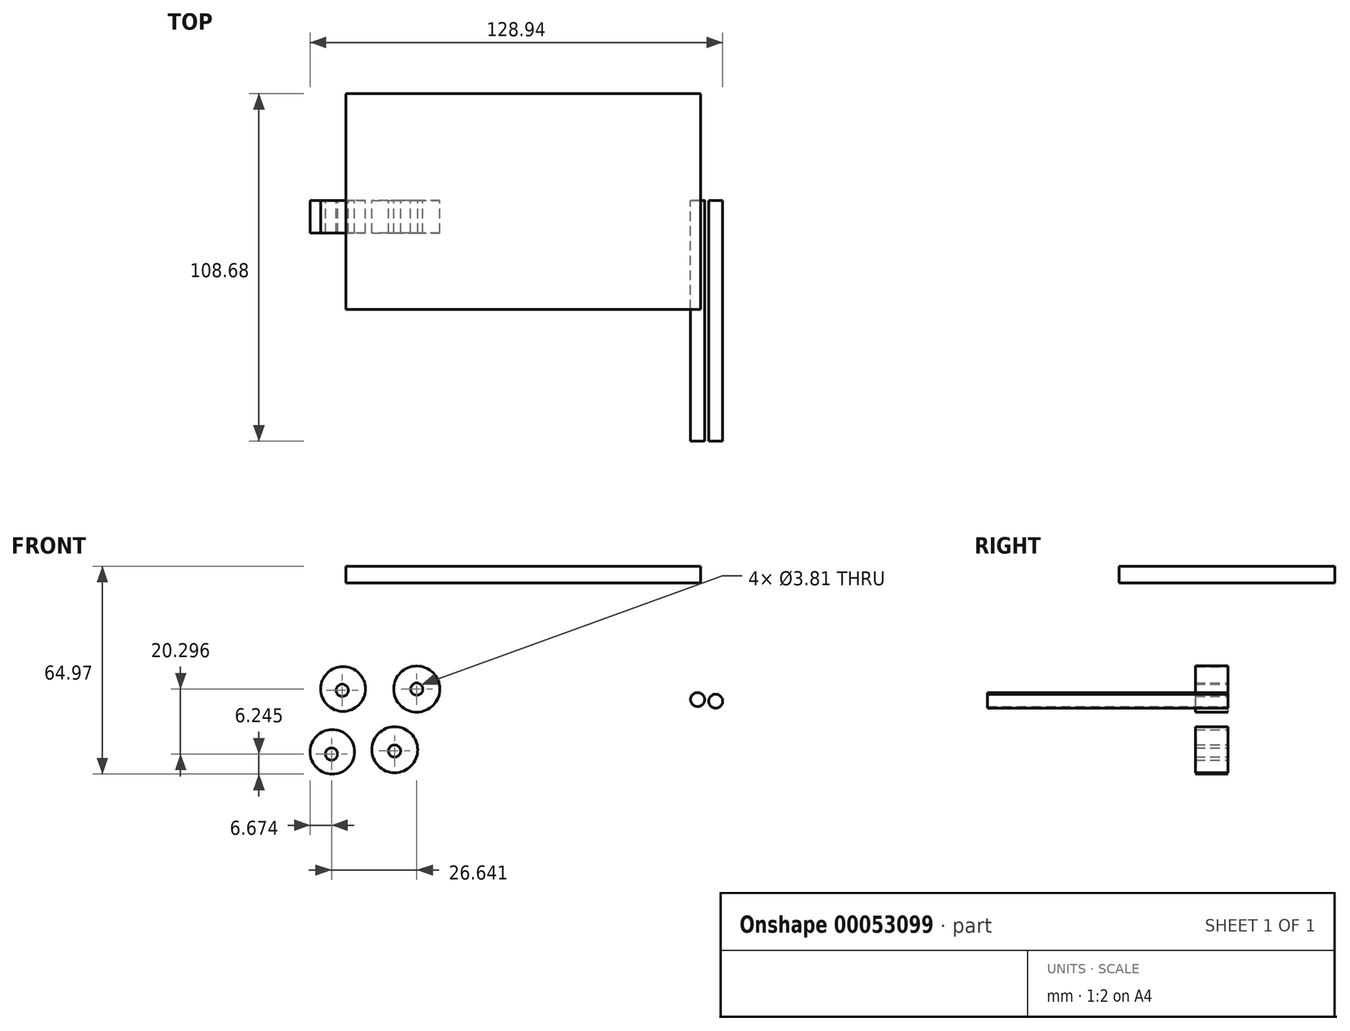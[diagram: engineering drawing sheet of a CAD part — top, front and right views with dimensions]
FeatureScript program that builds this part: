
annotation { "Feature Type Name" : "Feature", "Feature Type Description" : "" }
export const myFeature = defineFeature(function(context is Context, id is Id, definition is map)
    precondition{}
    {
        {
            var Q0;
            Q0=qCreatedBy(makeId("Top.planeOp"),FACE);
            var sketch = newSketch(context, id + "F0", { "sketchPlane" : qUnion([Q0])});
            skLineSegment(sketch, "E0.bottom", {"start": v(-58.44, 33.42) * mm, "end": v(52.35, 33.42) * mm});
            skLineSegment(sketch, "E0.top", {"start": v(-58.44, -34.06) * mm, "end": v(52.35, -34.06) * mm});
            skLineSegment(sketch, "E0.left", {"start": v(-58.44, 33.42) * mm, "end": v(-58.44, -34.06) * mm});
            skLineSegment(sketch, "E0.right", {"start": v(52.35, 33.42) * mm, "end": v(52.35, -34.06) * mm});
            skSolve(sketch);
        }
        {
            var Q0;
            Q0 = qSketchRegion(id + "F0", true);
            extrude(context, id + "F1", {"entities" : qUnion([Q0]), "depth" : 5.3 * mm});
        }
        {
            var Q0;
            Q0=qCreatedBy(makeId("Front.planeOp"),FACE);
            var sketch = newSketch(context, id + "F2", { "sketchPlane" : qUnion([Q0])});
            skCircle(sketch, "E1", {"center": v(57.1, -36.91) * mm, "radius": 2.18 * mm});
            skCircle(sketch, "E2", {"center": v(51.46, -36.4) * mm, "radius": 2.2 * mm});
            skSolve(sketch);
        }
        {
            var Q0;
            Q0 = qSketchRegion(id + "F2", true);
            extrude(context, id + "F3", {"entities" : qUnion([Q0]), "depth" : 75.26 * mm});
        }
        {
            var Q0;
            Q0=qCreatedBy(makeId("Front.planeOp"),FACE);
            var sketch = newSketch(context, id + "F4", { "sketchPlane" : qUnion([Q0])});
            skCircle(sketch, "E3", {"center": v(-53.68, -50.73) * mm, "radius": 7.69 * mm});
            skCircle(sketch, "E4", {"center": v(-34.72, -49.33) * mm, "radius": 8.01 * mm});
            skSolve(sketch);
        }
        {
            var Q0;
            Q0=makeQuery(id+"F4.imprint","IMPRINT",FACE,{"disambiguationData":[TD([[makeQuery(id+"F4.imprint","IMPRINT",EDGE,{"derivedFrom":sQuery(id+"F4.wireOp",EDGE,"E4")}),1.0]])]});
            var Q1;
            Q1=makeQuery(id+"F4.imprint","IMPRINT",FACE,{"disambiguationData":[TD([[makeQuery(id+"F4.imprint","IMPRINT",EDGE,{"derivedFrom":sQuery(id+"F4.wireOp",EDGE,"E3")}),1.0]])]});
            extrude(context, id + "F5", {"entities" : qUnion([Q0, Q1]), "depth" : 10.16 * mm});
        }
        {
            var Q0;
            Q0=makeQuery(id+"F5.opExtrude","SWEPT_BODY",BODY,{"disambiguationData":[OSD([sQuery(id+"F4.wireOp",EDGE,"E3")])]});
            deleteBodies(context, id + "F6", {"entities" : qUnion([Q0])});
        }
        {
            var Q0;
            Q0=makeQuery(id+"F5.opExtrude","SWEPT_BODY",BODY,{"disambiguationData":[OSD([sQuery(id+"F4.wireOp",EDGE,"E4")])]});
            deleteBodies(context, id + "F7", {"entities" : qUnion([Q0])});
        }
        {
            var Q0;
            Q0=qCreatedBy(makeId("Front.planeOp"),FACE);
            var sketch = newSketch(context, id + "F8", { "sketchPlane" : qUnion([Q0])});
            skCircle(sketch, "E5", {"center": v(-62.71, -52.75) * mm, "radius": 6.94 * mm});
            skCircle(sketch, "E6", {"center": v(-43.2, -52.1) * mm, "radius": 7.18 * mm});
            skCircle(sketch, "E7", {"center": v(-59.37, -33.1) * mm, "radius": 6.99 * mm});
            skCircle(sketch, "E8", {"center": v(-36.33, -33.14) * mm, "radius": 7.22 * mm});
            skSolve(sketch);
        }
        {
            var Q0;
            Q0 = qSketchRegion(id + "F8", true);
            extrude(context, id + "F9", {"entities" : qUnion([Q0]), "depth" : 10.16 * mm});
        }
        {
            var Q0;
            Q0=makeQuery(id+"F9.opExtrude","CAP_FACE",FACE,{"disambiguationData":[OSD([sQuery(id+"F8.wireOp",EDGE,"E8")])],"isStart":true});
            var sketch = newSketch(context, id + "F10", { "sketchPlane" : qUnion([Q0])});
            skPoint(sketch, "E9", {"position": v(59.62, -33.51) * mm});
            skPoint(sketch, "E10", {"position": v(62.98, -53.44) * mm});
            skPoint(sketch, "E11", {"position": v(36.33, -33.14) * mm});
            skPoint(sketch, "E12", {"position": v(43.27, -52.48) * mm});
            skSolve(sketch);
        }
        {
            var Q0;
            Q0=sQuery(id+"F10.wireOp",VERTEX,"E11");
            var Q1;
            Q1=sQuery(id+"F10.wireOp",VERTEX,"E9");
            var Q2;
            Q2=sQuery(id+"F10.wireOp",VERTEX,"E10");
            var Q3;
            Q3=sQuery(id+"F10.wireOp",VERTEX,"E12");
            var Q4;
            Q4=makeQuery(id+"F9.opExtrude","SWEPT_BODY",BODY,{"disambiguationData":[OSD([sQuery(id+"F8.wireOp",EDGE,"E8")])]});
            var Q5;
            Q5=makeQuery(id+"F9.opExtrude","SWEPT_BODY",BODY,{"disambiguationData":[OSD([sQuery(id+"F8.wireOp",EDGE,"E7")])]});
            var Q6;
            Q6=makeQuery(id+"F9.opExtrude","SWEPT_BODY",BODY,{"disambiguationData":[OSD([sQuery(id+"F8.wireOp",EDGE,"E5")])]});
            var Q7;
            Q7=makeQuery(id+"F9.opExtrude","SWEPT_BODY",BODY,{"disambiguationData":[OSD([sQuery(id+"F8.wireOp",EDGE,"E6")])]});
            hole(context, id + "F11", {"style" : HoleStyle.SIMPLE, "holeDiameter" : 3.8 * mm, "endStyle" : HoleEndStyle.THROUGH, "locations" : qUnion([Q0, Q1, Q2, Q3]), "scope" : qUnion([Q4, Q5, Q6, Q7])});
        }
    });
